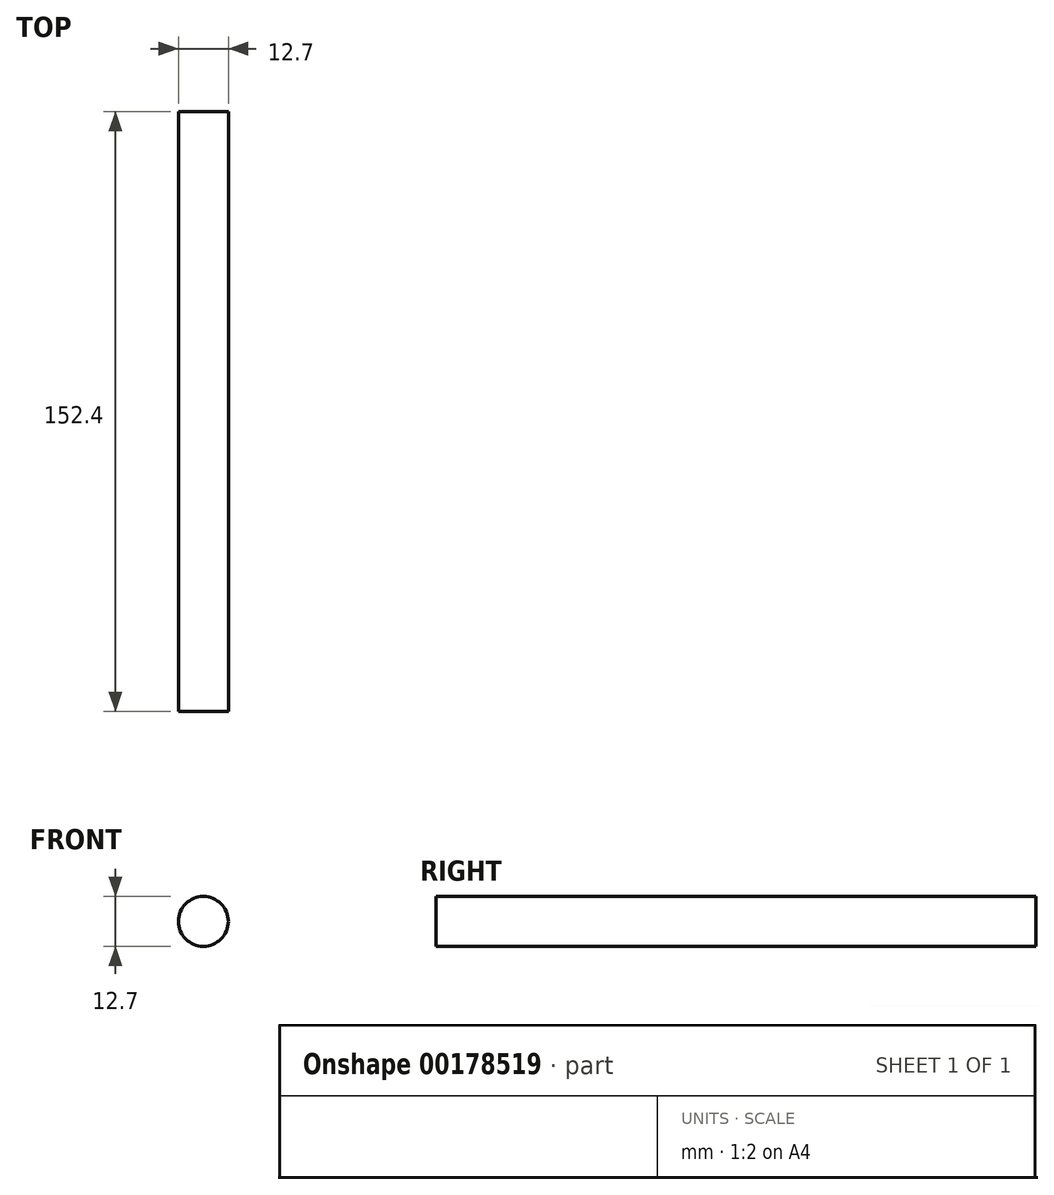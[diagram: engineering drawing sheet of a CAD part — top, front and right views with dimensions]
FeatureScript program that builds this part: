
annotation { "Feature Type Name" : "Feature", "Feature Type Description" : "" }
export const myFeature = defineFeature(function(context is Context, id is Id, definition is map)
    precondition{}
    {
        {
            var Q0;
            Q0=qCreatedBy(makeId("Front.planeOp"),FACE);
            var sketch = newSketch(context, id + "F0", { "sketchPlane" : qUnion([Q0])});
            skCircle(sketch, "E0", {"center": v(0, 0) * mm, "radius": 6.35 * mm});
            skSolve(sketch);
        }
        {
            var Q0;
            Q0=makeQuery(id+"F0.imprint","IMPRINT",FACE,{"disambiguationData":[TD([[makeQuery(id+"F0.imprint","IMPRINT",EDGE,{"derivedFrom":sQuery(id+"F0.wireOp",EDGE,"E0")}),1.0]])]});
            extrude(context, id + "F1", {"entities" : qUnion([Q0]), "depth" : 152.4 * mm});
        }
    });
